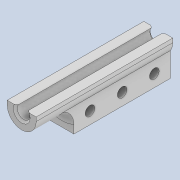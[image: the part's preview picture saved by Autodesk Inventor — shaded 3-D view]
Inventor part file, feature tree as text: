
AUTODESK INVENTOR PART (.ipt)
format: ipt  version: 2020 (Build 240168000, 168)  size: 186,368 bytes
history: native  units: mm
features: other x6, extrude x5, sketch x5, projected_geometry x4, reference x2, fillet x1, chamfer x1
ambient origin geometry x8: Origin, YZ Plane, XZ Plane, XY Plane, X Axis, Y Axis, Z Axis, Center Point
bodies: Solid1 (feature_tree)
feature tree (24):
  extrude  "Extrusion1"  Depth=1.0mm
  extrude  "Extrusion2"  Depth=1.8mm
  extrude  "Extrusion3"  Depth=1.8mm
  extrude  "Extrusion4"  Depth=12.0mm TaperAngle=0.0deg
  extrude  "Extrusion5"  Depth=3.0mm
  fillet  "Fillet1"  Radius=7.0mm
  chamfer  "Chamfer1"  Distance=12.0mm
  sketch  "Sketch1"  dims[d0=1.6mm d1=1.0mm]
  reference  "Reference1"
  sketch  "Sketch2"  dims[d2=0.5mm d3=1.8mm]
  projected_geometry  "Projected Loop1"
  sketch  "Sketch3"  dims[d4=0.5mm d5=1.8mm]
  reference  "Reference2"
  projected_geometry  "Projected Loop2"
  sketch  "Sketch4"  dims[d6=0.5mm d7=12.0mm d8=0.0mm]
  projected_geometry  "Projected Loop3"
  sketch  "Sketch5"  dims[d9=7.0mm d10=3.0mm d11=7.0mm d12=12.0mm d13=0.0mm d14=3.0mm d15=1.5mm d16=1.2mm d17=4.0mm d18=1.2mm d19=4.0mm d20=1.2mm d21=12.0mm d22=0.0mm d23=3.0mm d24=12.0mm d25=0.0mm d26=3.6mm d27=5.0mm d28=0.0mm d29=1.5mm d30=0.25mm d31=2.0mm d32=45.0deg]
  projected_geometry  "Projected Loop4"
  parser-record x2  (decoder bookkeeping rows leaked as tree rows — omitted from the tree; the rows remain in map.json)
  other  "bw_ass_1.iam"
  other  "bw_tube_0.8_1.6:1"
  other  "tip_3_ass.iam"
  other  "ext_shell_1:1"
note: 2 file-system paths scrubbed to <path> (originals preserved in map.json)
